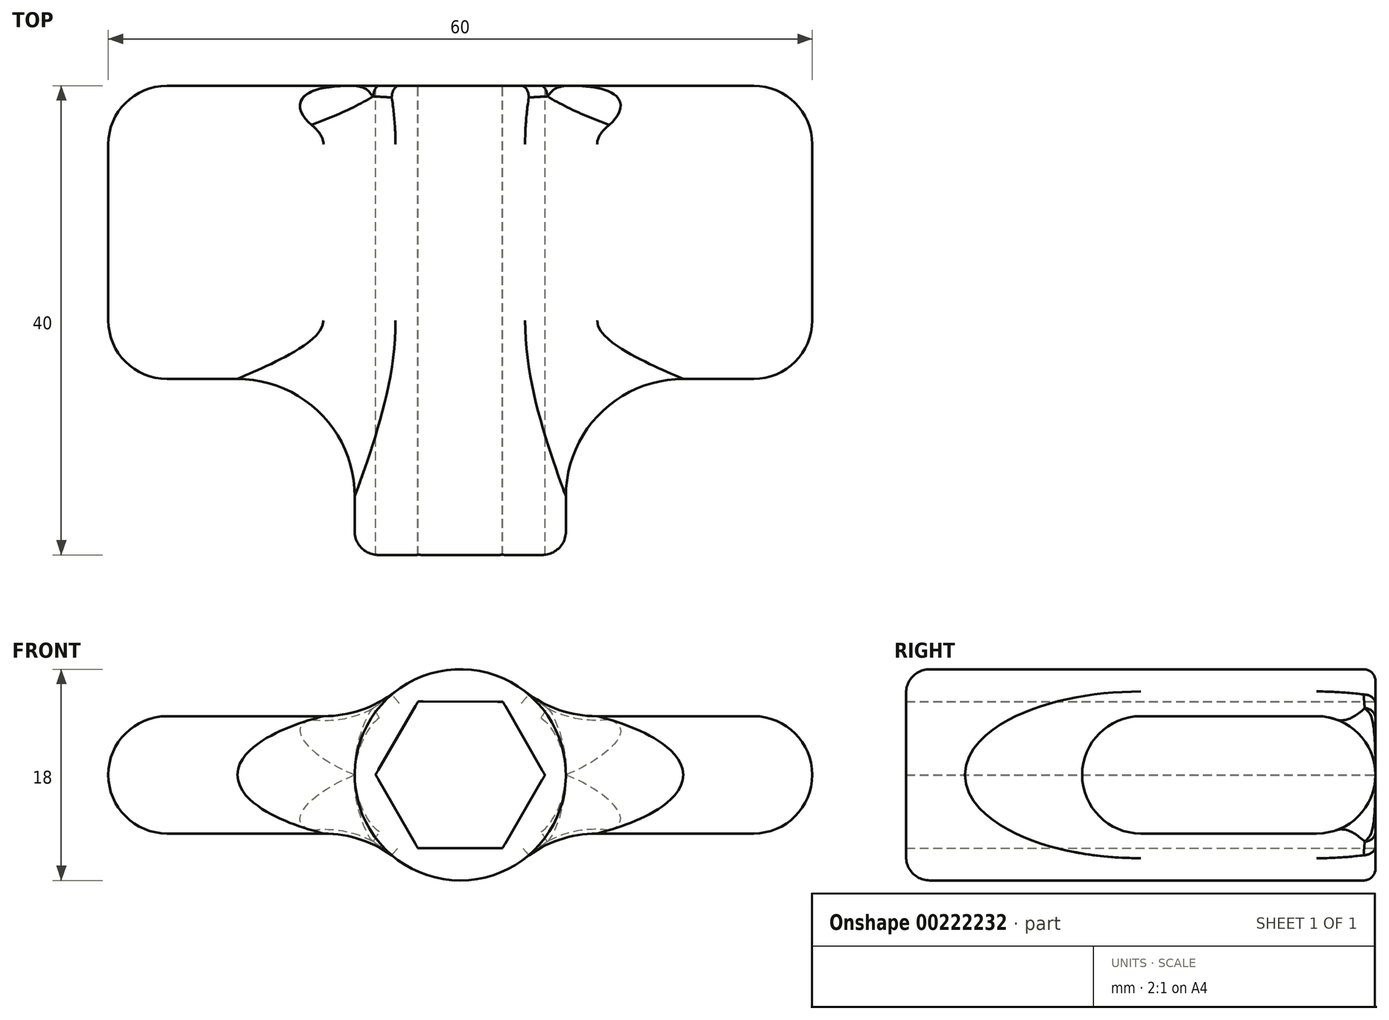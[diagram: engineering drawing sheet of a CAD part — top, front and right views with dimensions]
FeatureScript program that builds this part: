
annotation { "Feature Type Name" : "Feature", "Feature Type Description" : "" }
export const myFeature = defineFeature(function(context is Context, id is Id, definition is map)
    precondition{}
    {
        {
            var Q0;
            Q0=qCreatedBy(makeId("Front.planeOp"),FACE);
            var sketch = newSketch(context, id + "F0", { "sketchPlane" : qUnion([Q0])});
            skCircle(sketch, "E0.cCircle", {"center": v(0, 0) * mm, "radius": 6.25 * mm, "construction": true});
            skLineSegment(sketch, "E0.0", {"start": v(-7.22, 0.02) * mm, "end": v(-3.6, 6.26) * mm});
            skLineSegment(sketch, "E0.1", {"start": v(-3.6, 6.26) * mm, "end": v(3.62, 6.24) * mm});
            skLineSegment(sketch, "E0.2", {"start": v(3.62, 6.24) * mm, "end": v(7.22, -0.02) * mm});
            skLineSegment(sketch, "E0.3", {"start": v(7.22, -0.02) * mm, "end": v(3.6, -6.26) * mm});
            skLineSegment(sketch, "E0.4", {"start": v(3.6, -6.26) * mm, "end": v(-3.62, -6.24) * mm});
            skLineSegment(sketch, "E0.5", {"start": v(-3.62, -6.24) * mm, "end": v(-7.22, 0.02) * mm});
            skPoint(sketch, "E0.0.midPoint", {"position": v(-5.4, 3.14) * mm});
            skPoint(sketch, "E1", {"position": v(5.4, -3.14) * mm});
            skCircle(sketch, "E2", {"center": v(0, 0) * mm, "radius": 9 * mm});
            skPoint(sketch, "E3", {"position": v(-30, 0) * mm});
            skPoint(sketch, "E4", {"position": v(30, 0) * mm});
            skPoint(sketch, "E5", {"position": v(-30, 5) * mm});
            skPoint(sketch, "E6", {"position": v(30, 5) * mm});
            skPoint(sketch, "E7", {"position": v(30, -5) * mm});
            skPoint(sketch, "E8", {"position": v(-30, -5) * mm});
            skPoint(sketch, "E9", {"position": v(-7.48, 5) * mm});
            skPoint(sketch, "E10", {"position": v(-7.48, -5) * mm});
            skPoint(sketch, "E11", {"position": v(7.48, 5) * mm});
            skPoint(sketch, "E12", {"position": v(7.48, -5) * mm});
            skLineSegment(sketch, "E13", {"start": v(-25, 5) * mm, "end": v(-7.48, 5) * mm});
            skLineSegment(sketch, "E14", {"start": v(-30, 0) * mm, "end": v(-30, 0) * mm});
            skLineSegment(sketch, "E15", {"start": v(-25, -5) * mm, "end": v(-7.48, -5) * mm});
            skLineSegment(sketch, "E16", {"start": v(7.48, 5) * mm, "end": v(25, 5) * mm});
            skLineSegment(sketch, "E17", {"start": v(30, 0) * mm, "end": v(30, 0) * mm});
            skLineSegment(sketch, "E18", {"start": v(25, -5) * mm, "end": v(7.48, -5) * mm});
            skArc(sketch, "E19.filletArc", {"start": v(-25, 5) * mm, "mid": v(-28.54, 3.54) * mm, "end": v(-30, 0) * mm});
            skArc(sketch, "E20.filletArc", {"start": v(-30, 0) * mm, "mid": v(-28.54, -3.54) * mm, "end": v(-25, -5) * mm});
            skArc(sketch, "E21.filletArc", {"start": v(30, 0) * mm, "mid": v(28.54, 3.54) * mm, "end": v(25, 5) * mm});
            skArc(sketch, "E22.filletArc", {"start": v(25, -5) * mm, "mid": v(28.54, -3.54) * mm, "end": v(30, 0) * mm});
            skSolve(sketch);
        }
        {
            var Q0;
            Q0=makeQuery(id+"F0.imprint","IMPRINT",FACE,{"disambiguationData":[TD([[makeQuery(id+"F0.imprint","IMPRINT",EDGE,{"derivedFrom":sQuery(id+"F0.wireOp",EDGE,"E0.0")}),1.0]])]});
            extrude(context, id + "F1", {"entities" : qUnion([Q0]), "depth" : 40 * mm});
        }
        {
            var Q0;
            {var subQ0=sQuery(id+"F0.wireOp",EDGE,"E13");Q0=makeQuery(id+"F0.imprint","IMPRINT",FACE,{"disambiguationData":[TD([[makeQuery(id+"F0.imprint","IMPRINT",EDGE,{"derivedFrom":subQ0}),-1.0]])]});}
            var Q1;
            {var subQ0=sQuery(id+"F0.wireOp",EDGE,"E16");Q1=makeQuery(id+"F0.imprint","IMPRINT",FACE,{"disambiguationData":[TD([[makeQuery(id+"F0.imprint","IMPRINT",EDGE,{"derivedFrom":subQ0}),-1.0]])]});}
            extrude(context, id + "F2", {"entities" : qUnion([Q0, Q1]), "operationType" : NewBodyOperationType.ADD, "depth" : 25 * mm});
        }
        {
            var Q0;
            Q0=makeQuery(id+"F2.opExtrude","CAP_EDGE",EDGE,{"disambiguationData":[OSD([sQuery(id+"F0.wireOp",EDGE,"E15")])],"isStart":true});
            var Q1;
            Q1=makeQuery(id+"F2.opExtrude","CAP_EDGE",EDGE,{"disambiguationData":[OSD([sQuery(id+"F0.wireOp",EDGE,"E18")])],"isStart":true});
            var Q2;
            Q2=makeQuery(id+"F2.opExtrude","CAP_EDGE",EDGE,{"disambiguationData":[OSD([sQuery(id+"F0.wireOp",EDGE,"E16")])],"isStart":false});
            var Q3;
            Q3=makeQuery(id+"F2.opExtrude","CAP_EDGE",EDGE,{"disambiguationData":[OSD([sQuery(id+"F0.wireOp",EDGE,"E13")])],"isStart":false});
            fillet(context, id + "F3", {"entities" : qUnion([Q0, Q1, Q2, Q3]), "radius" : 5 * mm, "tangentPropagation" : true, "allowEdgeOverflow" : false});
        }
        {
            var Q0;
            Q0=makeQuery(id+"F3.opFillet","BLEND_EDGE",EDGE,{"blendedFrom":[makeQuery(id+"F2.opExtrude","CAP_EDGE",EDGE,{"disambiguationData":[OSD([sQuery(id+"F0.wireOp",EDGE,"E15")])],"isStart":false}),makeQuery(id+"F1.opExtrude","SWEPT_FACE",FACE,{"disambiguationData":[OSD([sQuery(id+"F0.wireOp",EDGE,"E2")])]})],"blendedInto":[makeQuery(id+"F1.opExtrude","SWEPT_FACE",FACE,{"disambiguationData":[OSD([sQuery(id+"F0.wireOp",EDGE,"E2")])]})]});
            var Q1;
            Q1=makeQuery(id+"F3.opFillet","BLEND_EDGE",EDGE,{"blendedFrom":[makeQuery(id+"F2.opExtrude","CAP_EDGE",EDGE,{"disambiguationData":[OSD([sQuery(id+"F0.wireOp",EDGE,"E18")])],"isStart":false}),makeQuery(id+"F1.opExtrude","SWEPT_FACE",FACE,{"disambiguationData":[OSD([sQuery(id+"F0.wireOp",EDGE,"E2")])]})],"blendedInto":[makeQuery(id+"F1.opExtrude","SWEPT_FACE",FACE,{"disambiguationData":[OSD([sQuery(id+"F0.wireOp",EDGE,"E2")])]})]});
            fillet(context, id + "F4", {"entities" : qUnion([Q0, Q1]), "radius" : 10 * mm, "tangentPropagation" : true, "allowEdgeOverflow" : false});
        }
        {
            var Q0;
            Q0=makeQuery(id+"F1.opExtrude","CAP_EDGE",EDGE,{"disambiguationData":[OSD([sQuery(id+"F0.wireOp",EDGE,"E2")])],"isStart":false});
            fillet(context, id + "F5", {"entities" : qUnion([Q0]), "radius" : 2 * mm, "tangentPropagation" : true, "allowEdgeOverflow" : false});
        }
        {
            var Q0;
            {var subQ0=sQuery(id+"F0.wireOp",EDGE,"E13");var subQ1=sQuery(id+"F0.wireOp",EDGE,"E2");Q0=makeQuery(id+"F2.boolean.opBoolean","SPLIT",EDGE,{"disambiguationData":[TD([makeQuery(id+"F2.opExtrude","SWEPT_FACE",FACE,{"disambiguationData":[OSD([subQ0])]})])],"derivedFrom":makeQuery(id+"F1.opExtrude","CAP_EDGE",EDGE,{"disambiguationData":[OSD([subQ1])],"isStart":true})});}
            var Q1;
            {var subQ0=sQuery(id+"F0.wireOp",EDGE,"E15");var subQ1=sQuery(id+"F0.wireOp",EDGE,"E2");Q1=makeQuery(id+"F2.boolean.opBoolean","SPLIT",EDGE,{"disambiguationData":[TD([makeQuery(id+"F2.opExtrude","SWEPT_FACE",FACE,{"disambiguationData":[OSD([subQ0])]})])],"derivedFrom":makeQuery(id+"F1.opExtrude","CAP_EDGE",EDGE,{"disambiguationData":[OSD([subQ1])],"isStart":true})});}
            var Q2;
            {var subQ0=sQuery(id+"F0.wireOp",EDGE,"E18");var subQ1=sQuery(id+"F0.wireOp",EDGE,"E2");Q2=makeQuery(id+"F4.opFillet","BLEND_EDGE",EDGE,{"blendedFrom":[makeQuery(id+"F3.opFillet","BLEND_EDGE",EDGE,{"blendedFrom":[makeQuery(id+"F2.opExtrude","CAP_EDGE",EDGE,{"disambiguationData":[OSD([subQ0])],"isStart":true}),makeQuery(id+"F1.opExtrude","SWEPT_FACE",FACE,{"disambiguationData":[OSD([subQ1])]})],"blendedInto":[makeQuery(id+"F1.opExtrude","SWEPT_FACE",FACE,{"disambiguationData":[OSD([subQ1])]})]}),makeQuery(id+"F2.boolean.opBoolean","MERGE",FACE,{"derivedFrom":[makeQuery(id+"F1.opExtrude","CAP_FACE",FACE,{"disambiguationData":[OSD([sQuery(id+"F0.wireOp",EDGE,"E0.0"),sQuery(id+"F0.wireOp",EDGE,"E0.1"),sQuery(id+"F0.wireOp",EDGE,"E0.2"),sQuery(id+"F0.wireOp",EDGE,"E0.3"),sQuery(id+"F0.wireOp",EDGE,"E0.4"),sQuery(id+"F0.wireOp",EDGE,"E0.5"),subQ1])],"isStart":true}),makeQuery(id+"F2.opExtrude","CAP_FACE",FACE,{"disambiguationData":[OSD([subQ1,sQuery(id+"F0.wireOp",EDGE,"E13"),sQuery(id+"F0.wireOp",EDGE,"E15"),sQuery(id+"F0.wireOp",EDGE,"E19.filletArc"),sQuery(id+"F0.wireOp",EDGE,"E20.filletArc")])],"isStart":true}),makeQuery(id+"F2.opExtrude","CAP_FACE",FACE,{"disambiguationData":[OSD([subQ1,sQuery(id+"F0.wireOp",EDGE,"E16"),subQ0,sQuery(id+"F0.wireOp",EDGE,"E21.filletArc"),sQuery(id+"F0.wireOp",EDGE,"E22.filletArc")])],"isStart":true})]})],"blendedInto":[makeQuery(id+"F2.boolean.opBoolean","MERGE",FACE,{"derivedFrom":[makeQuery(id+"F1.opExtrude","CAP_FACE",FACE,{"disambiguationData":[OSD([sQuery(id+"F0.wireOp",EDGE,"E0.0"),sQuery(id+"F0.wireOp",EDGE,"E0.1"),sQuery(id+"F0.wireOp",EDGE,"E0.2"),sQuery(id+"F0.wireOp",EDGE,"E0.3"),sQuery(id+"F0.wireOp",EDGE,"E0.4"),sQuery(id+"F0.wireOp",EDGE,"E0.5"),subQ1])],"isStart":true}),makeQuery(id+"F2.opExtrude","CAP_FACE",FACE,{"disambiguationData":[OSD([subQ1,sQuery(id+"F0.wireOp",EDGE,"E13"),sQuery(id+"F0.wireOp",EDGE,"E15"),sQuery(id+"F0.wireOp",EDGE,"E19.filletArc"),sQuery(id+"F0.wireOp",EDGE,"E20.filletArc")])],"isStart":true}),makeQuery(id+"F2.opExtrude","CAP_FACE",FACE,{"disambiguationData":[OSD([subQ1,sQuery(id+"F0.wireOp",EDGE,"E16"),subQ0,sQuery(id+"F0.wireOp",EDGE,"E21.filletArc"),sQuery(id+"F0.wireOp",EDGE,"E22.filletArc")])],"isStart":true})]})]});}
            var Q3;
            {var subQ0=sQuery(id+"F0.wireOp",EDGE,"E16");var subQ1=sQuery(id+"F0.wireOp",EDGE,"E2");Q3=makeQuery(id+"F4.opFillet","BLEND_EDGE",EDGE,{"blendedFrom":[makeQuery(id+"F3.opFillet","BLEND_EDGE",EDGE,{"blendedFrom":[makeQuery(id+"F2.opExtrude","CAP_EDGE",EDGE,{"disambiguationData":[OSD([subQ0])],"isStart":true}),makeQuery(id+"F1.opExtrude","SWEPT_FACE",FACE,{"disambiguationData":[OSD([subQ1])]})],"blendedInto":[makeQuery(id+"F1.opExtrude","SWEPT_FACE",FACE,{"disambiguationData":[OSD([subQ1])]})]}),makeQuery(id+"F2.boolean.opBoolean","MERGE",FACE,{"derivedFrom":[makeQuery(id+"F1.opExtrude","CAP_FACE",FACE,{"disambiguationData":[OSD([sQuery(id+"F0.wireOp",EDGE,"E0.0"),sQuery(id+"F0.wireOp",EDGE,"E0.1"),sQuery(id+"F0.wireOp",EDGE,"E0.2"),sQuery(id+"F0.wireOp",EDGE,"E0.3"),sQuery(id+"F0.wireOp",EDGE,"E0.4"),sQuery(id+"F0.wireOp",EDGE,"E0.5"),subQ1])],"isStart":true}),makeQuery(id+"F2.opExtrude","CAP_FACE",FACE,{"disambiguationData":[OSD([subQ1,sQuery(id+"F0.wireOp",EDGE,"E13"),sQuery(id+"F0.wireOp",EDGE,"E15"),sQuery(id+"F0.wireOp",EDGE,"E19.filletArc"),sQuery(id+"F0.wireOp",EDGE,"E20.filletArc")])],"isStart":true}),makeQuery(id+"F2.opExtrude","CAP_FACE",FACE,{"disambiguationData":[OSD([subQ1,subQ0,sQuery(id+"F0.wireOp",EDGE,"E18"),sQuery(id+"F0.wireOp",EDGE,"E21.filletArc"),sQuery(id+"F0.wireOp",EDGE,"E22.filletArc")])],"isStart":true})]})],"blendedInto":[makeQuery(id+"F2.boolean.opBoolean","MERGE",FACE,{"derivedFrom":[makeQuery(id+"F1.opExtrude","CAP_FACE",FACE,{"disambiguationData":[OSD([sQuery(id+"F0.wireOp",EDGE,"E0.0"),sQuery(id+"F0.wireOp",EDGE,"E0.1"),sQuery(id+"F0.wireOp",EDGE,"E0.2"),sQuery(id+"F0.wireOp",EDGE,"E0.3"),sQuery(id+"F0.wireOp",EDGE,"E0.4"),sQuery(id+"F0.wireOp",EDGE,"E0.5"),subQ1])],"isStart":true}),makeQuery(id+"F2.opExtrude","CAP_FACE",FACE,{"disambiguationData":[OSD([subQ1,sQuery(id+"F0.wireOp",EDGE,"E13"),sQuery(id+"F0.wireOp",EDGE,"E15"),sQuery(id+"F0.wireOp",EDGE,"E19.filletArc"),sQuery(id+"F0.wireOp",EDGE,"E20.filletArc")])],"isStart":true}),makeQuery(id+"F2.opExtrude","CAP_FACE",FACE,{"disambiguationData":[OSD([subQ1,subQ0,sQuery(id+"F0.wireOp",EDGE,"E18"),sQuery(id+"F0.wireOp",EDGE,"E21.filletArc"),sQuery(id+"F0.wireOp",EDGE,"E22.filletArc")])],"isStart":true})]})]});}
            var Q4;
            {var subQ0=sQuery(id+"F0.wireOp",EDGE,"E2");var subQ1=sQuery(id+"F0.wireOp",EDGE,"E15");Q4=makeQuery(id+"F4.opFillet","BLEND_EDGE",EDGE,{"blendedFrom":[makeQuery(id+"F3.opFillet","BLEND_EDGE",EDGE,{"blendedFrom":[makeQuery(id+"F2.opExtrude","CAP_EDGE",EDGE,{"disambiguationData":[OSD([subQ1])],"isStart":true}),makeQuery(id+"F1.opExtrude","SWEPT_FACE",FACE,{"disambiguationData":[OSD([subQ0])]})],"blendedInto":[makeQuery(id+"F1.opExtrude","SWEPT_FACE",FACE,{"disambiguationData":[OSD([subQ0])]})]}),makeQuery(id+"F2.boolean.opBoolean","MERGE",FACE,{"derivedFrom":[makeQuery(id+"F1.opExtrude","CAP_FACE",FACE,{"disambiguationData":[OSD([sQuery(id+"F0.wireOp",EDGE,"E0.0"),sQuery(id+"F0.wireOp",EDGE,"E0.1"),sQuery(id+"F0.wireOp",EDGE,"E0.2"),sQuery(id+"F0.wireOp",EDGE,"E0.3"),sQuery(id+"F0.wireOp",EDGE,"E0.4"),sQuery(id+"F0.wireOp",EDGE,"E0.5"),subQ0])],"isStart":true}),makeQuery(id+"F2.opExtrude","CAP_FACE",FACE,{"disambiguationData":[OSD([subQ0,sQuery(id+"F0.wireOp",EDGE,"E13"),subQ1,sQuery(id+"F0.wireOp",EDGE,"E19.filletArc"),sQuery(id+"F0.wireOp",EDGE,"E20.filletArc")])],"isStart":true}),makeQuery(id+"F2.opExtrude","CAP_FACE",FACE,{"disambiguationData":[OSD([subQ0,sQuery(id+"F0.wireOp",EDGE,"E16"),sQuery(id+"F0.wireOp",EDGE,"E18"),sQuery(id+"F0.wireOp",EDGE,"E21.filletArc"),sQuery(id+"F0.wireOp",EDGE,"E22.filletArc")])],"isStart":true})]})],"blendedInto":[makeQuery(id+"F2.boolean.opBoolean","MERGE",FACE,{"derivedFrom":[makeQuery(id+"F1.opExtrude","CAP_FACE",FACE,{"disambiguationData":[OSD([sQuery(id+"F0.wireOp",EDGE,"E0.0"),sQuery(id+"F0.wireOp",EDGE,"E0.1"),sQuery(id+"F0.wireOp",EDGE,"E0.2"),sQuery(id+"F0.wireOp",EDGE,"E0.3"),sQuery(id+"F0.wireOp",EDGE,"E0.4"),sQuery(id+"F0.wireOp",EDGE,"E0.5"),subQ0])],"isStart":true}),makeQuery(id+"F2.opExtrude","CAP_FACE",FACE,{"disambiguationData":[OSD([subQ0,sQuery(id+"F0.wireOp",EDGE,"E13"),subQ1,sQuery(id+"F0.wireOp",EDGE,"E19.filletArc"),sQuery(id+"F0.wireOp",EDGE,"E20.filletArc")])],"isStart":true}),makeQuery(id+"F2.opExtrude","CAP_FACE",FACE,{"disambiguationData":[OSD([subQ0,sQuery(id+"F0.wireOp",EDGE,"E16"),sQuery(id+"F0.wireOp",EDGE,"E18"),sQuery(id+"F0.wireOp",EDGE,"E21.filletArc"),sQuery(id+"F0.wireOp",EDGE,"E22.filletArc")])],"isStart":true})]})]});}
            var Q5;
            {var subQ0=sQuery(id+"F0.wireOp",EDGE,"E2");var subQ1=sQuery(id+"F0.wireOp",EDGE,"E13");Q5=makeQuery(id+"F4.opFillet","BLEND_EDGE",EDGE,{"blendedFrom":[makeQuery(id+"F3.opFillet","BLEND_EDGE",EDGE,{"blendedFrom":[makeQuery(id+"F2.opExtrude","CAP_EDGE",EDGE,{"disambiguationData":[OSD([subQ1])],"isStart":true}),makeQuery(id+"F1.opExtrude","SWEPT_FACE",FACE,{"disambiguationData":[OSD([subQ0])]})],"blendedInto":[makeQuery(id+"F1.opExtrude","SWEPT_FACE",FACE,{"disambiguationData":[OSD([subQ0])]})]}),makeQuery(id+"F2.boolean.opBoolean","MERGE",FACE,{"derivedFrom":[makeQuery(id+"F1.opExtrude","CAP_FACE",FACE,{"disambiguationData":[OSD([sQuery(id+"F0.wireOp",EDGE,"E0.0"),sQuery(id+"F0.wireOp",EDGE,"E0.1"),sQuery(id+"F0.wireOp",EDGE,"E0.2"),sQuery(id+"F0.wireOp",EDGE,"E0.3"),sQuery(id+"F0.wireOp",EDGE,"E0.4"),sQuery(id+"F0.wireOp",EDGE,"E0.5"),subQ0])],"isStart":true}),makeQuery(id+"F2.opExtrude","CAP_FACE",FACE,{"disambiguationData":[OSD([subQ0,subQ1,sQuery(id+"F0.wireOp",EDGE,"E15"),sQuery(id+"F0.wireOp",EDGE,"E19.filletArc"),sQuery(id+"F0.wireOp",EDGE,"E20.filletArc")])],"isStart":true}),makeQuery(id+"F2.opExtrude","CAP_FACE",FACE,{"disambiguationData":[OSD([subQ0,sQuery(id+"F0.wireOp",EDGE,"E16"),sQuery(id+"F0.wireOp",EDGE,"E18"),sQuery(id+"F0.wireOp",EDGE,"E21.filletArc"),sQuery(id+"F0.wireOp",EDGE,"E22.filletArc")])],"isStart":true})]})],"blendedInto":[makeQuery(id+"F2.boolean.opBoolean","MERGE",FACE,{"derivedFrom":[makeQuery(id+"F1.opExtrude","CAP_FACE",FACE,{"disambiguationData":[OSD([sQuery(id+"F0.wireOp",EDGE,"E0.0"),sQuery(id+"F0.wireOp",EDGE,"E0.1"),sQuery(id+"F0.wireOp",EDGE,"E0.2"),sQuery(id+"F0.wireOp",EDGE,"E0.3"),sQuery(id+"F0.wireOp",EDGE,"E0.4"),sQuery(id+"F0.wireOp",EDGE,"E0.5"),subQ0])],"isStart":true}),makeQuery(id+"F2.opExtrude","CAP_FACE",FACE,{"disambiguationData":[OSD([subQ0,subQ1,sQuery(id+"F0.wireOp",EDGE,"E15"),sQuery(id+"F0.wireOp",EDGE,"E19.filletArc"),sQuery(id+"F0.wireOp",EDGE,"E20.filletArc")])],"isStart":true}),makeQuery(id+"F2.opExtrude","CAP_FACE",FACE,{"disambiguationData":[OSD([subQ0,sQuery(id+"F0.wireOp",EDGE,"E16"),sQuery(id+"F0.wireOp",EDGE,"E18"),sQuery(id+"F0.wireOp",EDGE,"E21.filletArc"),sQuery(id+"F0.wireOp",EDGE,"E22.filletArc")])],"isStart":true})]})]});}
            fillet(context, id + "F6", {"entities" : qUnion([Q0, Q1, Q2, Q3, Q4, Q5]), "radius" : 1 * mm, "tangentPropagation" : true, "allowEdgeOverflow" : false});
        }
    });
